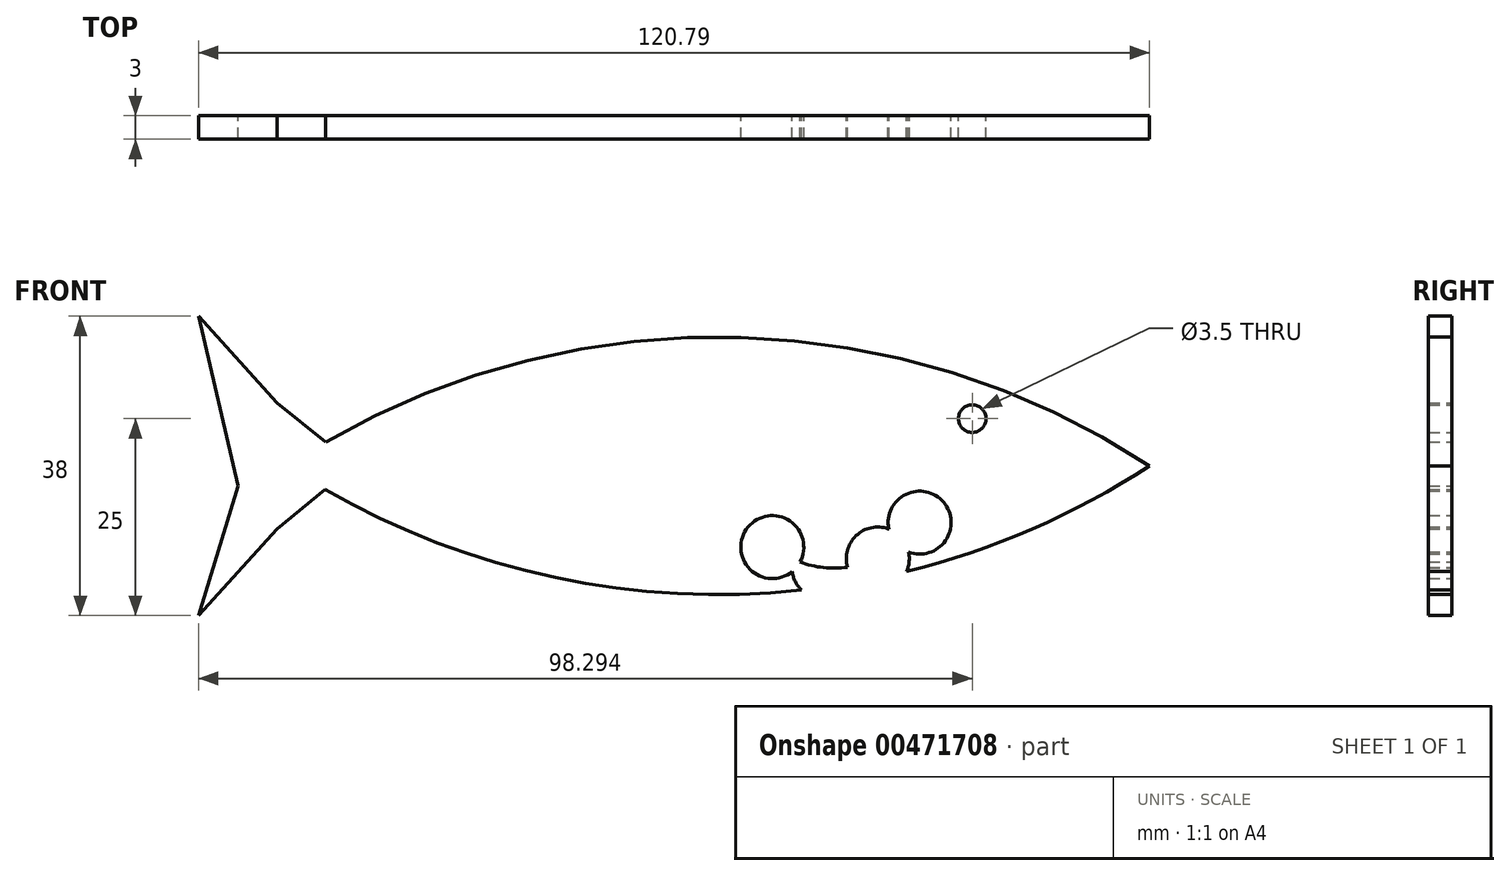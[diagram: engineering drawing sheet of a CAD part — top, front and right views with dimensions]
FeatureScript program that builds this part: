
annotation { "Feature Type Name" : "Feature", "Feature Type Description" : "" }
export const myFeature = defineFeature(function(context is Context, id is Id, definition is map)
    precondition{}
    {
        {
            var Q0;
            Q0=qCreatedBy(makeId("Front.planeOp"),FACE);
            var sketch = newSketch(context, id + "F0", { "sketchPlane" : qUnion([Q0])});
            skLineSegment(sketch, "E0.bottom", {"start": v(0, 0) * mm, "end": v(80, 0) * mm});
            skLineSegment(sketch, "E0.top", {"start": v(0, 16) * mm, "end": v(80, 16) * mm});
            skLineSegment(sketch, "E0.left", {"start": v(0, 0) * mm, "end": v(0, 16) * mm});
            skLineSegment(sketch, "E0.right", {"start": v(80, 0) * mm, "end": v(80, 16) * mm});
            skArc(sketch, "E1", {"start": v(94.8, 8) * mm, "mid": v(40, 24.35) * mm, "end": v(-14.8, 8) * mm});
            skArc(sketch, "E2", {"start": v(-14.8, 8) * mm, "mid": v(40, -8.35) * mm, "end": v(94.8, 8) * mm});
            skLineSegment(sketch, "E3.right", {"start": v(-16, 0) * mm, "end": v(-16, 16) * mm});
            skLineSegment(sketch, "E4", {"start": v(-16, 16) * mm, "end": v(-26, 27) * mm});
            skLineSegment(sketch, "E5", {"start": v(-26, -11) * mm, "end": v(-16, 0) * mm});
            skCircle(sketch, "E6", {"center": v(46.9, -2.32) * mm, "radius": 4 * mm});
            skCircle(sketch, "E7", {"center": v(53.4, -4.92) * mm, "radius": 4 * mm});
            skCircle(sketch, "E8", {"center": v(60.3, -3.78) * mm, "radius": 4 * mm});
            skCircle(sketch, "E9", {"center": v(65.6, 0.78) * mm, "radius": 4 * mm});
            skCircle(sketch, "E10", {"center": v(54.8, 8) * mm, "radius": 13 * mm});
            skCircle(sketch, "E11", {"center": v(72.3, 14) * mm, "radius": 1.75 * mm});
            skLineSegment(sketch, "E12", {"start": v(-26, 27) * mm, "end": v(-20.96, 5.45) * mm});
            skLineSegment(sketch, "E13", {"start": v(-20.96, 5.45) * mm, "end": v(-26, -11) * mm});
            skLineSegment(sketch, "E14", {"start": v(-16, 16) * mm, "end": v(-9.82, 11.06) * mm});
            skLineSegment(sketch, "E15", {"start": v(-16, 0) * mm, "end": v(-9.9, 4.99) * mm});
            skSolve(sketch);
        }
        {
            var Q0;
            Q0=makeQuery(id+"F0.imprint","IMPRINT",FACE,{"disambiguationData":[TD([[makeQuery(id+"F0.imprint","IMPRINT",EDGE,{"derivedFrom":sQuery(id+"F0.wireOp",EDGE,"E3.right")}),1.0]])]});
            var Q1;
            {var subQ1=sQuery(id+"F0.wireOp",EDGE,"E3.bottom");Q1=makeQuery(id+"F0.imprint","IMPRINT",FACE,{"disambiguationData":[TD([[makeQuery(id+"F0.imprint","IMPRINT",EDGE,{"derivedFrom":subQ1}),-1.0]])]});}
            var Q2;
            {var subQ0=sQuery(id+"F0.wireOp",EDGE,"E3.left");Q2=makeQuery(id+"F0.imprint","IMPRINT",FACE,{"disambiguationData":[TD([[makeQuery(id+"F0.imprint","IMPRINT",EDGE,{"derivedFrom":subQ0}),1.0]])]});}
            var Q3;
            {var subQ0=sQuery(id+"F0.wireOp",EDGE,"E3.left");Q3=makeQuery(id+"F0.imprint","IMPRINT",FACE,{"disambiguationData":[TD([[makeQuery(id+"F0.imprint","IMPRINT",EDGE,{"derivedFrom":subQ0}),-1.0]])]});}
            var Q4;
            {var subQ1=sQuery(id+"F0.wireOp",EDGE,"E0.top");var subQ3=sQuery(id+"F0.wireOp",EDGE,"E10");var subQ4=makeQuery(id+"F0.imprint","INTERSECT",VERTEX,{"disambiguationData":[OD(0.0)],"derivedFrom":[subQ1,subQ3]});Q4=makeQuery(id+"F0.imprint","IMPRINT",FACE,{"disambiguationData":[TD([[makeQuery(id+"F0.imprint","IMPRINT",EDGE,{"disambiguationData":[TD([[subQ4,1.0]])],"derivedFrom":subQ3}),-1.0]])]});}
            var Q5;
            {var subQ5=sQuery(id+"F0.wireOp",EDGE,"E6");var subQ6=sQuery(id+"F0.wireOp",EDGE,"E0.bottom");var subQ7=makeQuery(id+"F0.imprint","INTERSECT",VERTEX,{"disambiguationData":[OD(0.0)],"derivedFrom":[subQ6,subQ5]});Q5=makeQuery(id+"F0.imprint","IMPRINT",FACE,{"disambiguationData":[TD([[makeQuery(id+"F0.imprint","IMPRINT",EDGE,{"disambiguationData":[TD([[subQ7,-1.0]])],"derivedFrom":subQ5}),-1.0]])]});}
            var Q6;
            {var subQ0=sQuery(id+"F0.wireOp",EDGE,"E6");var subQ1=sQuery(id+"F0.wireOp",EDGE,"E0.bottom");var subQ2=makeQuery(id+"F0.imprint","INTERSECT",VERTEX,{"disambiguationData":[OD(1.0)],"derivedFrom":[subQ1,subQ0]});Q6=makeQuery(id+"F0.imprint","IMPRINT",FACE,{"disambiguationData":[TD([[makeQuery(id+"F0.imprint","IMPRINT",EDGE,{"disambiguationData":[TD([[subQ2,-1.0]])],"derivedFrom":subQ1}),1.0]])]});}
            var Q7;
            {var subQ0=sQuery(id+"F0.wireOp",EDGE,"E6");var subQ1=sQuery(id+"F0.wireOp",EDGE,"E0.bottom");var subQ2=makeQuery(id+"F0.imprint","INTERSECT",VERTEX,{"disambiguationData":[OD(1.0)],"derivedFrom":[subQ1,subQ0]});Q7=makeQuery(id+"F0.imprint","IMPRINT",FACE,{"disambiguationData":[TD([[makeQuery(id+"F0.imprint","IMPRINT",EDGE,{"disambiguationData":[TD([[subQ2,-1.0]])],"derivedFrom":subQ1}),-1.0]])]});}
            var Q8;
            {var subQ0=sQuery(id+"F0.wireOp",EDGE,"E0.right");Q8=makeQuery(id+"F0.imprint","IMPRINT",FACE,{"disambiguationData":[TD([[makeQuery(id+"F0.imprint","IMPRINT",EDGE,{"derivedFrom":subQ0}),1.0]])]});}
            var Q9;
            {var subQ0=sQuery(id+"F0.wireOp",EDGE,"E8");var subQ1=sQuery(id+"F0.wireOp",EDGE,"E2");var subQ2=makeQuery(id+"F0.imprint","INTERSECT",VERTEX,{"disambiguationData":[OD(1.0)],"derivedFrom":[subQ1,subQ0]});Q9=makeQuery(id+"F0.imprint","IMPRINT",FACE,{"disambiguationData":[TD([[makeQuery(id+"F0.imprint","IMPRINT",EDGE,{"disambiguationData":[TD([[subQ2,-1.0]])],"derivedFrom":subQ0}),-1.0]])]});}
            var Q10;
            {var subQ0=sQuery(id+"F0.wireOp",EDGE,"E0.right");Q10=makeQuery(id+"F0.imprint","IMPRINT",FACE,{"disambiguationData":[TD([[makeQuery(id+"F0.imprint","IMPRINT",EDGE,{"derivedFrom":subQ0}),-1.0]])]});}
            var Q11;
            {var subQ0=sQuery(id+"F0.wireOp",EDGE,"E10");var subQ1=sQuery(id+"F0.wireOp",EDGE,"E0.top");var subQ2=makeQuery(id+"F0.imprint","INTERSECT",VERTEX,{"disambiguationData":[OD(0.0)],"derivedFrom":[subQ1,subQ0]});Q11=makeQuery(id+"F0.imprint","IMPRINT",FACE,{"disambiguationData":[TD([[makeQuery(id+"F0.imprint","IMPRINT",EDGE,{"disambiguationData":[TD([[subQ2,-1.0]])],"derivedFrom":subQ1}),1.0]])]});}
            var Q12;
            {var subQ3=sQuery(id+"F0.wireOp",EDGE,"E6");var subQ7=sQuery(id+"F0.wireOp",EDGE,"E10");var subQ8=makeQuery(id+"F0.imprint","INTERSECT",VERTEX,{"disambiguationData":[OD(0.0)],"derivedFrom":[subQ3,subQ7]});Q12=makeQuery(id+"F0.imprint","IMPRINT",FACE,{"disambiguationData":[TD([[makeQuery(id+"F0.imprint","IMPRINT",EDGE,{"disambiguationData":[TD([[subQ8,-1.0]])],"derivedFrom":subQ3}),-1.0]])]});}
            var Q13;
            {var subQ0=sQuery(id+"F0.wireOp",EDGE,"E0.left");Q13=makeQuery(id+"F0.imprint","IMPRINT",FACE,{"disambiguationData":[TD([[makeQuery(id+"F0.imprint","IMPRINT",EDGE,{"derivedFrom":subQ0}),-1.0]])]});}
            var Q14;
            {var subQ4=sQuery(id+"F0.wireOp",EDGE,"E0.left");Q14=makeQuery(id+"F0.imprint","IMPRINT",FACE,{"disambiguationData":[TD([[makeQuery(id+"F0.imprint","IMPRINT",EDGE,{"derivedFrom":subQ4}),1.0]])]});}
            var Q15;
            Q15=makeQuery(id+"F0.imprint","IMPRINT",FACE,{"disambiguationData":[TD([[makeQuery(id+"F0.imprint","IMPRINT",EDGE,{"derivedFrom":sQuery(id+"F0.wireOp",EDGE,"E3.right")}),-1.0]])]});
            extrude(context, id + "F1", {"entities" : qUnion([Q0, Q1, Q2, Q3, Q4, Q5, Q6, Q7, Q8, Q9, Q10, Q11, Q12, Q13, Q14, Q15]), "depth" : 3 * mm});
        }
    });
